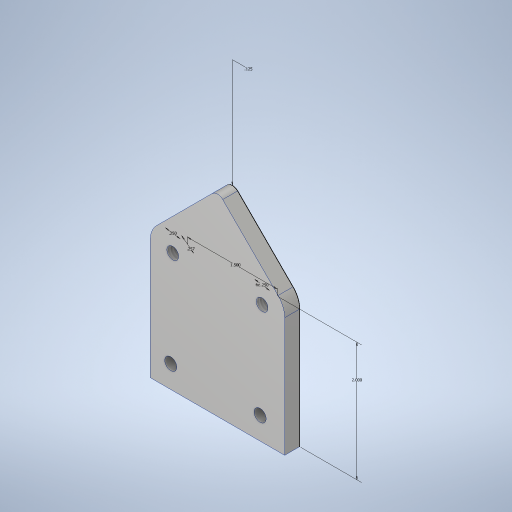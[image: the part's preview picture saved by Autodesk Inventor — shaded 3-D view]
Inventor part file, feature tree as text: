
AUTODESK INVENTOR PART (.ipt)
format: ipt  version: 2023.4 (Build 274418000, 418)  size: 267,776 bytes
history: native  units: in
note: dims shown in document units (in); Inventor stores cm internally (conversion verified against a paired STEP export)
features: sketch x2, hole x2, extrude x1
ambient origin geometry x8: Origin, YZ Plane, XZ Plane, XY Plane, X Axis, Y Axis, Z Axis, Center Point
bodies: Solid1 (feature_tree)
feature tree (5):
  sketch  "Sketch1"  dims[d0=0.257in d1=1.5in]
  extrude  "Extrusion1"  Depth=1.5in
  hole  "Hole1"  [1 undecoded]
  hole  "Hole2"  [1 undecoded]
  sketch  "Sketch2"  dims[d2=0.25in d3=0.25in d4=2.0in d5=0.125in d6=0.25in d7=0.0in d8=1.5in d9=0.375in d10=0.201in d11=0.75in d12=0.385in d13=0.25in d14=0.5635in d15=1.0in d16=0.8108in d17=0.196in d18=0.5in d19=0.385in d20=0.25in d21=0.5635in d22=1.0in d23=0.8108in]
note: 2 required parameter values undecoded (feature->parameter linkage not recoverable at this tier; creation-order binding heuristic only, values carry confidence <= 0.55)
